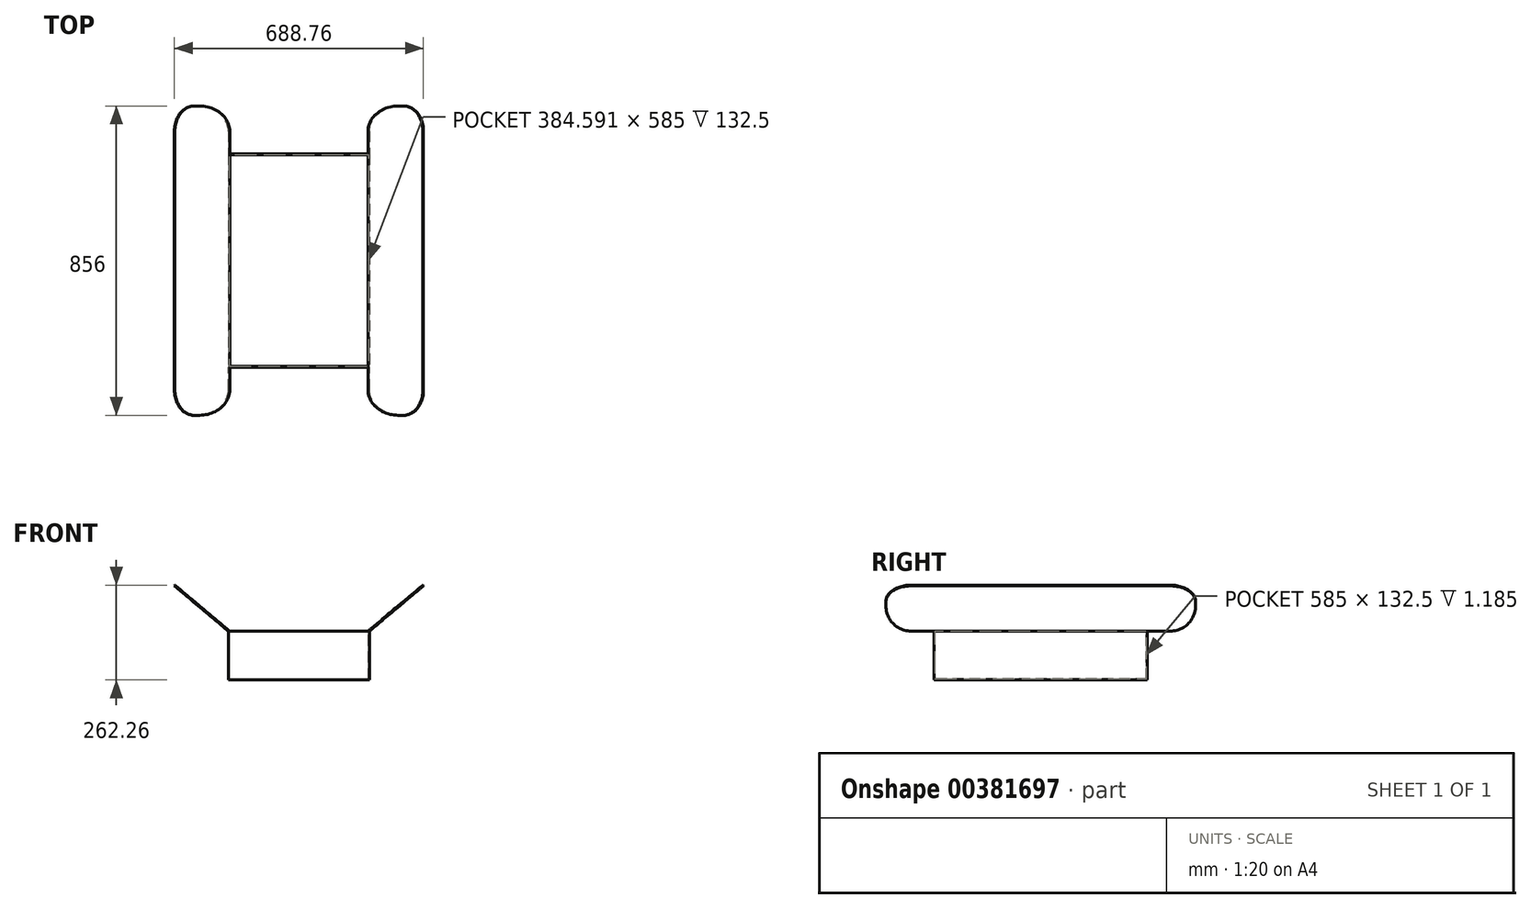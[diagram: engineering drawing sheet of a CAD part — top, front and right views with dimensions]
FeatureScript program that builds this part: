
annotation { "Feature Type Name" : "Feature", "Feature Type Description" : "" }
export const myFeature = defineFeature(function(context is Context, id is Id, definition is map)
    precondition{}
    {
        {
            var Q0;
            Q0=qCreatedBy(makeId("Front.planeOp"),FACE);
            var sketch = newSketch(context, id + "F0", { "sketchPlane" : qUnion([Q0])});
            skLineSegment(sketch, "E0.bottom", {"start": v(195, -67.5) * mm, "end": v(-195, -67.5) * mm});
            skLineSegment(sketch, "E0.top", {"start": v(195, 67.5) * mm, "end": v(-195, 67.5) * mm});
            skLineSegment(sketch, "E0.left", {"start": v(195, -67.5) * mm, "end": v(195, 67.5) * mm});
            skLineSegment(sketch, "E0.right", {"start": v(-195, -67.5) * mm, "end": v(-195, 67.5) * mm});
            skPoint(sketch, "E0.middle", {"position": v(0, 0) * mm});
            skSolve(sketch);
        }
        {
            var Q0;
            Q0 = qSketchRegion(id + "F0", true);
            extrude(context, id + "F1", {"entities" : qUnion([Q0]), "oppositeDirection" : true, "depth" : 590 * mm});
        }
        {
            var Q0;
            Q0=makeQuery(id+"F1.opExtrude","SWEPT_FACE",FACE,{"disambiguationData":[OSD([sQuery(id+"F0.wireOp",EDGE,"E0.top")])]});
            var sketch = newSketch(context, id + "F2", { "sketchPlane" : qUnion([Q0])});
            skLineSegment(sketch, "E1", {"start": v(0, 0) * mm, "end": v(0, 590) * mm, "construction": true});
            skLineSegment(sketch, "E2.bottom", {"start": v(-192.3, 587.5) * mm, "end": v(192.3, 587.5) * mm});
            skLineSegment(sketch, "E2.top", {"start": v(-192.3, 2.5) * mm, "end": v(192.3, 2.5) * mm});
            skLineSegment(sketch, "E2.left", {"start": v(-192.3, 587.5) * mm, "end": v(-192.3, 2.5) * mm});
            skLineSegment(sketch, "E2.right", {"start": v(192.3, 587.5) * mm, "end": v(192.3, 2.5) * mm});
            skPoint(sketch, "E2.middle", {"position": v(0, 295) * mm});
            skSolve(sketch);
        }
        {
            var Q0;
            Q0 = qSketchRegion(id + "F2", true);
            extrude(context, id + "F3", {"entities" : qUnion([Q0]), "operationType" : NewBodyOperationType.REMOVE, "oppositeDirection" : true, "depth" : 132.5 * mm});
        }
        {
            var Q0;
            Q0=makeQuery(id+"F1.opExtrude","CAP_FACE",FACE,{"disambiguationData":[OSD([sQuery(id+"F0.wireOp",EDGE,"E0.bottom"),sQuery(id+"F0.wireOp",EDGE,"E0.top"),sQuery(id+"F0.wireOp",EDGE,"E0.left"),sQuery(id+"F0.wireOp",EDGE,"E0.right")])],"isStart":true});
            var sketch = newSketch(context, id + "F4", { "sketchPlane" : qUnion([Q0])});
            skLineSegment(sketch, "E3", {"start": v(195, 67.5) * mm, "end": v(344.38, 192.84) * mm});
            skLineSegment(sketch, "E4", {"start": v(344.38, 192.84) * mm, "end": v(342.77, 194.76) * mm});
            skLineSegment(sketch, "E5", {"start": v(342.77, 194.76) * mm, "end": v(191.11, 67.5) * mm});
            skLineSegment(sketch, "E6", {"start": v(0, -67.5) * mm, "end": v(0, 67.5) * mm, "construction": true});
            skLineSegment(sketch, "E7.MirrorCS", {"start": v(-195, 67.5) * mm, "end": v(-344.38, 192.84) * mm});
            skLineSegment(sketch, "E8.MirrorCS", {"start": v(-342.77, 194.76) * mm, "end": v(-191.11, 67.5) * mm});
            skLineSegment(sketch, "E9.MirrorCS", {"start": v(-344.38, 192.84) * mm, "end": v(-342.77, 194.76) * mm});
            skSolve(sketch);
        }
        {
            var Q0;
            {var subQ0=sQuery(id+"F4.wireOp",EDGE,"E7.MirrorCS");Q0=makeQuery(id+"F4.imprint","IMPRINT",FACE,{"disambiguationData":[TD([[makeQuery(id+"F4.imprint","IMPRINT",EDGE,{"derivedFrom":subQ0}),-1.0]])]});}
            var Q1;
            {var subQ0=sQuery(id+"F4.wireOp",EDGE,"E3");Q1=makeQuery(id+"F4.imprint","IMPRINT",FACE,{"disambiguationData":[TD([[makeQuery(id+"F4.imprint","IMPRINT",EDGE,{"derivedFrom":subQ0}),1.0]])]});}
            extrude(context, id + "F5", {"entities" : qUnion([Q0, Q1]), "operationType" : NewBodyOperationType.ADD, "oppositeDirection" : true, "depth" : 590 * mm});
        }
        {
            var Q0;
            {var subQ0=sQuery(id+"F0.wireOp",EDGE,"E0.top");Q0=makeQuery(id+"F5.boolean.opBoolean","MERGE",FACE,{"derivedFrom":[makeQuery(id+"F1.opExtrude","CAP_FACE",FACE,{"disambiguationData":[OSD([sQuery(id+"F0.wireOp",EDGE,"E0.bottom"),subQ0,sQuery(id+"F0.wireOp",EDGE,"E0.left"),sQuery(id+"F0.wireOp",EDGE,"E0.right")])],"isStart":false}),makeQuery(id+"F5.opExtrude","CAP_FACE",FACE,{"disambiguationData":[OSD([subQ0,sQuery(id+"F4.wireOp",EDGE,"E3"),sQuery(id+"F4.wireOp",EDGE,"E4"),sQuery(id+"F4.wireOp",EDGE,"E5")])],"isStart":false}),makeQuery(id+"F5.opExtrude","CAP_FACE",FACE,{"disambiguationData":[OSD([subQ0,sQuery(id+"F4.wireOp",EDGE,"E7.MirrorCS"),sQuery(id+"F4.wireOp",EDGE,"E8.MirrorCS"),sQuery(id+"F4.wireOp",EDGE,"E9.MirrorCS")])],"isStart":false})]});}
            var sketch = newSketch(context, id + "F6", { "sketchPlane" : qUnion([Q0])});
            skLineSegment(sketch, "E10", {"start": v(344.38, 192.84) * mm, "end": v(342.77, 194.76) * mm});
            skLineSegment(sketch, "E11", {"start": v(342.77, 194.76) * mm, "end": v(191.11, 67.5) * mm});
            skLineSegment(sketch, "E12", {"start": v(191.11, 67.5) * mm, "end": v(195, 67.5) * mm});
            skLineSegment(sketch, "E13", {"start": v(195, 67.5) * mm, "end": v(344.38, 192.84) * mm});
            skLineSegment(sketch, "E14", {"start": v(0, -67.5) * mm, "end": v(0, 67.5) * mm, "construction": true});
            skLineSegment(sketch, "E15.MirrorCS", {"start": v(-195, 67.5) * mm, "end": v(-344.38, 192.84) * mm});
            skLineSegment(sketch, "E16.MirrorCS", {"start": v(-342.77, 194.76) * mm, "end": v(-191.11, 67.5) * mm});
            skLineSegment(sketch, "E17.MirrorCS", {"start": v(-191.11, 67.5) * mm, "end": v(-195, 67.5) * mm});
            skLineSegment(sketch, "E18.MirrorCS", {"start": v(-344.38, 192.84) * mm, "end": v(-342.77, 194.76) * mm});
            skSolve(sketch);
        }
        {
            var Q0;
            Q0 = qSketchRegion(id + "F6", true);
            extrude(context, id + "F7", {"entities" : qUnion([Q0]), "operationType" : NewBodyOperationType.ADD, "depth" : 133 * mm});
        }
        {
            var Q0;
            Q0=makeQuery(id+"F7.opExtrude","CAP_EDGE",EDGE,{"disambiguationData":[OSD([sQuery(id+"F6.wireOp",EDGE,"E18.MirrorCS")])],"isStart":false});
            var Q1;
            Q1=makeQuery(id+"F7.opExtrude","CAP_EDGE",EDGE,{"disambiguationData":[OSD([sQuery(id+"F6.wireOp",EDGE,"E17.MirrorCS")])],"isStart":false});
            var Q2;
            Q2=makeQuery(id+"F7.opExtrude","CAP_EDGE",EDGE,{"disambiguationData":[OSD([sQuery(id+"F6.wireOp",EDGE,"E12")])],"isStart":false});
            var Q3;
            Q3=makeQuery(id+"F7.opExtrude","CAP_EDGE",EDGE,{"disambiguationData":[OSD([sQuery(id+"F6.wireOp",EDGE,"E10")])],"isStart":false});
            fillet(context, id + "F8", {"entities" : qUnion([Q0, Q1, Q2, Q3]), "radius" : 70 * mm, "tangentPropagation" : true, "allowEdgeOverflow" : false});
        }
        {
            var Q0;
            {var subQ0=sQuery(id+"F0.wireOp",EDGE,"E0.top");Q0=makeQuery(id+"F5.boolean.opBoolean","MERGE",FACE,{"derivedFrom":[makeQuery(id+"F1.opExtrude","CAP_FACE",FACE,{"disambiguationData":[OSD([sQuery(id+"F0.wireOp",EDGE,"E0.bottom"),subQ0,sQuery(id+"F0.wireOp",EDGE,"E0.left"),sQuery(id+"F0.wireOp",EDGE,"E0.right")])],"isStart":true}),makeQuery(id+"F5.opExtrude","CAP_FACE",FACE,{"disambiguationData":[OSD([subQ0,sQuery(id+"F4.wireOp",EDGE,"E3"),sQuery(id+"F4.wireOp",EDGE,"E4"),sQuery(id+"F4.wireOp",EDGE,"E5")])],"isStart":true}),makeQuery(id+"F5.opExtrude","CAP_FACE",FACE,{"disambiguationData":[OSD([subQ0,sQuery(id+"F4.wireOp",EDGE,"E7.MirrorCS"),sQuery(id+"F4.wireOp",EDGE,"E8.MirrorCS"),sQuery(id+"F4.wireOp",EDGE,"E9.MirrorCS")])],"isStart":true})]});}
            var sketch = newSketch(context, id + "F9", { "sketchPlane" : qUnion([Q0])});
            skLineSegment(sketch, "E19", {"start": v(191.11, 67.5) * mm, "end": v(342.77, 194.76) * mm});
            skLineSegment(sketch, "E20", {"start": v(342.77, 194.76) * mm, "end": v(344.38, 192.84) * mm});
            skLineSegment(sketch, "E21", {"start": v(344.38, 192.84) * mm, "end": v(195, 67.5) * mm});
            skLineSegment(sketch, "E22", {"start": v(195, 67.5) * mm, "end": v(191.11, 67.5) * mm});
            skLineSegment(sketch, "E23", {"start": v(-191.11, 67.5) * mm, "end": v(-342.77, 194.76) * mm});
            skLineSegment(sketch, "E24", {"start": v(-342.77, 194.76) * mm, "end": v(-344.38, 192.84) * mm});
            skLineSegment(sketch, "E25", {"start": v(-344.38, 192.84) * mm, "end": v(-195, 67.5) * mm});
            skLineSegment(sketch, "E26", {"start": v(-195, 67.5) * mm, "end": v(-191.11, 67.5) * mm});
            skSolve(sketch);
        }
        {
            var Q0;
            Q0 = qSketchRegion(id + "F9", true);
            extrude(context, id + "F10", {"entities" : qUnion([Q0]), "operationType" : NewBodyOperationType.ADD, "depth" : 133 * mm});
        }
        {
            var Q0;
            Q0=makeQuery(id+"F10.opExtrude","CAP_EDGE",EDGE,{"disambiguationData":[OSD([sQuery(id+"F9.wireOp",EDGE,"E24")])],"isStart":false});
            var Q1;
            Q1=makeQuery(id+"F10.opExtrude","CAP_EDGE",EDGE,{"disambiguationData":[OSD([sQuery(id+"F9.wireOp",EDGE,"E26")])],"isStart":false});
            var Q2;
            Q2=makeQuery(id+"F10.opExtrude","CAP_EDGE",EDGE,{"disambiguationData":[OSD([sQuery(id+"F9.wireOp",EDGE,"E22")])],"isStart":false});
            var Q3;
            Q3=makeQuery(id+"F10.opExtrude","CAP_EDGE",EDGE,{"disambiguationData":[OSD([sQuery(id+"F9.wireOp",EDGE,"E20")])],"isStart":false});
            fillet(context, id + "F11", {"entities" : qUnion([Q0, Q1, Q2, Q3]), "radius" : 70 * mm, "tangentPropagation" : true, "allowEdgeOverflow" : false});
        }
    });
